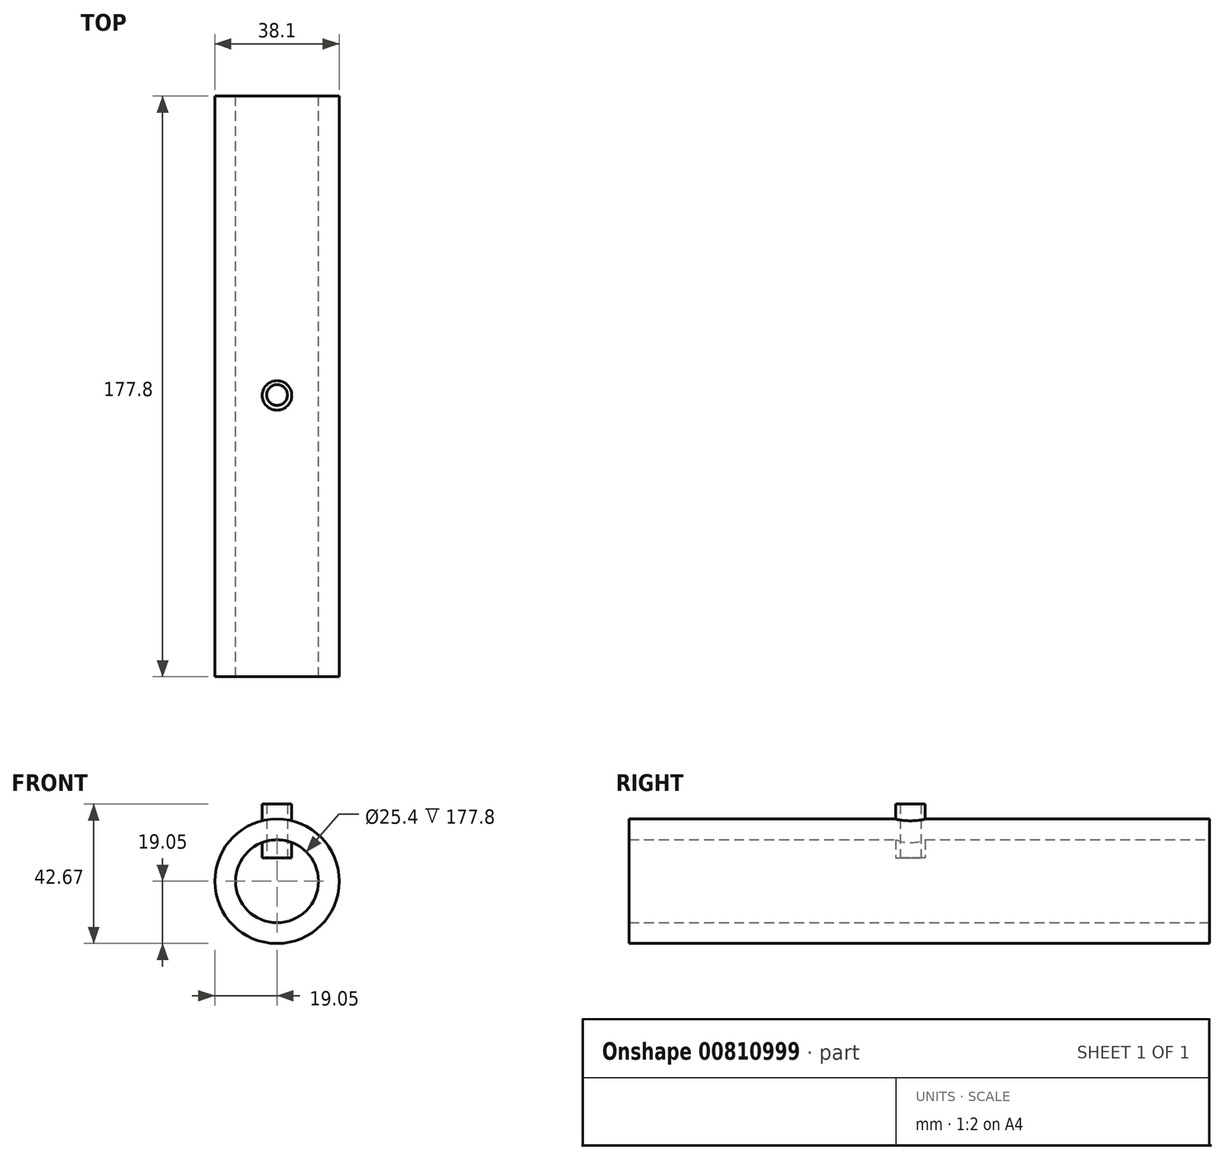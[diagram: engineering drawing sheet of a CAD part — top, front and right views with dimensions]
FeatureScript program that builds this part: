
annotation { "Feature Type Name" : "Feature", "Feature Type Description" : "" }
export const myFeature = defineFeature(function(context is Context, id is Id, definition is map)
    precondition{}
    {
        {
            var Q0;
            Q0=qCreatedBy(makeId("Front.planeOp"),FACE);
            var sketch = newSketch(context, id + "F0", { "sketchPlane" : qUnion([Q0])});
            skCircle(sketch, "E0", {"center": v(0, 0) * mm, "radius": 19.05 * mm});
            skSolve(sketch);
        }
        {
            var Q0;
            Q0 = qSketchRegion(id + "F0", true);
            extrude(context, id + "F1", {"entities" : qUnion([Q0]), "depth" : 177.8 * mm, "offsetDistance" : 25.4 * mm});
        }
        {
            var Q0;
            Q0=qCreatedBy(makeId("Front.planeOp"),FACE);
            var sketch = newSketch(context, id + "F2", { "sketchPlane" : qUnion([Q0])});
            skCircle(sketch, "E1", {"center": v(0, 0) * mm, "radius": 12.7 * mm});
            skSolve(sketch);
        }
        {
            var Q0;
            Q0 = qSketchRegion(id + "F2", true);
            extrude(context, id + "F3", {"entities" : qUnion([Q0]), "operationType" : NewBodyOperationType.REMOVE, "depth" : 177.8 * mm, "offsetDistance" : 25.4 * mm});
        }
        {
            var Q0;
            Q0=qCreatedBy(makeId("Top.planeOp"),FACE);
            var sketch = newSketch(context, id + "F4", { "sketchPlane" : qUnion([Q0])});
            skCircle(sketch, "E2", {"center": v(0, -91.66) * mm, "radius": 4.53 * mm});
            skSolve(sketch);
        }
        {
            var Q0;
            Q0 = qSketchRegion(id + "F4", true);
            extrude(context, id + "F5", {"entities" : qUnion([Q0]), "operationType" : NewBodyOperationType.ADD, "depth" : 23.62 * mm, "offsetDistance" : 25.4 * mm, "hasSecondDirection" : true, "secondDirectionOppositeDirection" : false, "secondDirectionDepth" : 7.11 * mm});
        }
        {
            var Q0;
            Q0=qCreatedBy(makeId("Top.planeOp"),FACE);
            var sketch = newSketch(context, id + "F6", { "sketchPlane" : qUnion([Q0])});
            skCircle(sketch, "E3", {"center": v(0, -91.52) * mm, "radius": 3.18 * mm});
            skSolve(sketch);
        }
        {
            var Q0;
            Q0 = qSketchRegion(id + "F6", true);
            extrude(context, id + "F7", {"entities" : qUnion([Q0]), "operationType" : NewBodyOperationType.REMOVE, "depth" : 24.38 * mm, "offsetDistance" : 25.4 * mm, "hasSecondDirection" : true, "secondDirectionOppositeDirection" : false, "secondDirectionDepth" : 6.6 * mm});
        }
    });
